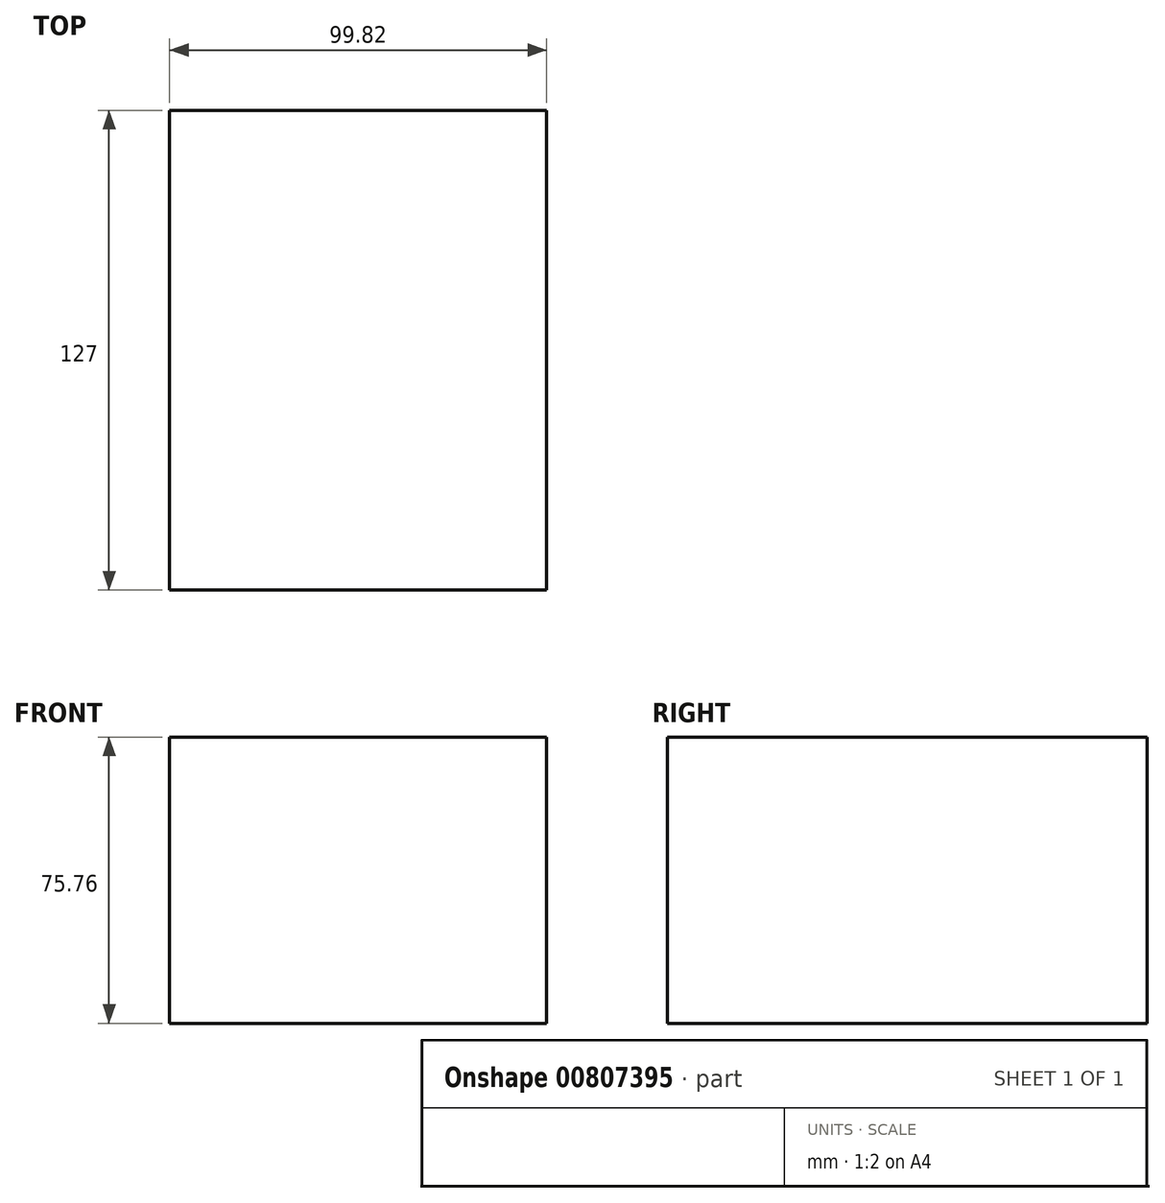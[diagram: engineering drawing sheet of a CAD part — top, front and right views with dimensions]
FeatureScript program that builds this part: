
annotation { "Feature Type Name" : "Feature", "Feature Type Description" : "" }
export const myFeature = defineFeature(function(context is Context, id is Id, definition is map)
    precondition{}
    {
        {
            var Q0;
            Q0=qCreatedBy(makeId("Front.planeOp"),FACE);
            var sketch = newSketch(context, id + "F0", { "sketchPlane" : qUnion([Q0])});
            skLineSegment(sketch, "E0.bottom", {"start": v(-49.91, 37.88) * mm, "end": v(49.91, 37.88) * mm});
            skLineSegment(sketch, "E0.top", {"start": v(-49.91, -37.88) * mm, "end": v(49.91, -37.88) * mm});
            skLineSegment(sketch, "E0.left", {"start": v(-49.91, 37.88) * mm, "end": v(-49.91, -37.88) * mm});
            skLineSegment(sketch, "E0.right", {"start": v(49.91, 37.88) * mm, "end": v(49.91, -37.88) * mm});
            skPoint(sketch, "E0.middle", {"position": v(0, 0) * mm});
            skSolve(sketch);
        }
        {
            var Q0;
            Q0=makeQuery(id+"F0.imprint","IMPRINT",FACE,{"disambiguationData":[TD([[makeQuery(id+"F0.imprint","IMPRINT",EDGE,{"derivedFrom":sQuery(id+"F0.wireOp",EDGE,"E0.bottom")}),-1.0]])]});
            extrude(context, id + "F1", {"entities" : qUnion([Q0]), "endBound" : BoundingType.SYMMETRIC, "depth" : 127 * mm, "offsetDistance" : 25.4 * mm});
        }
    });
